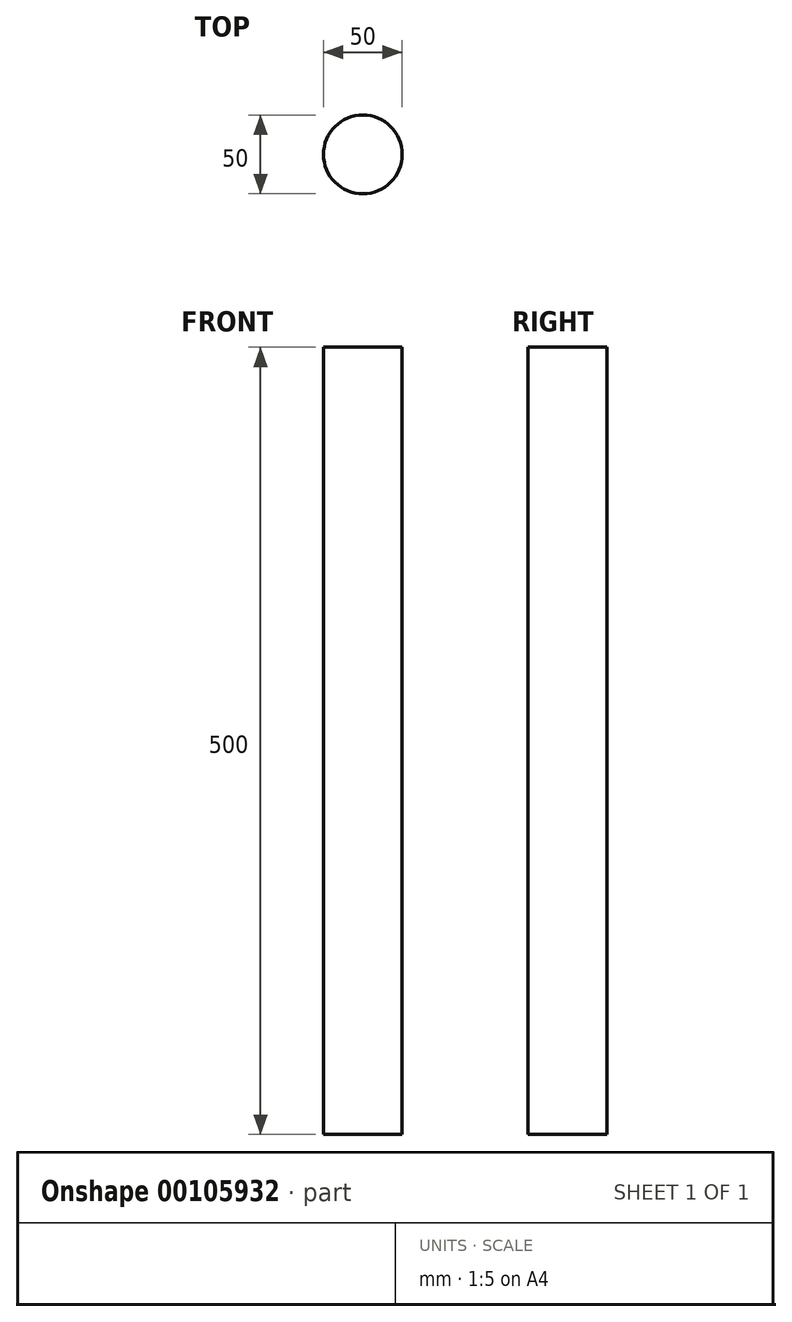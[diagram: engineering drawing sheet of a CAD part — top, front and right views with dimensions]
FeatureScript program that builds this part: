
annotation { "Feature Type Name" : "Feature", "Feature Type Description" : "" }
export const myFeature = defineFeature(function(context is Context, id is Id, definition is map)
    precondition{}
    {
        {
            var Q0;
            Q0=qCreatedBy(makeId("Top.planeOp"),FACE);
            var sketch = newSketch(context, id + "F0", { "sketchPlane" : qUnion([Q0])});
            skCircle(sketch, "E0", {"center": v(0, 0) * mm, "radius": 25 * mm});
            skSolve(sketch);
        }
        {
            var Q0;
            Q0=makeQuery(id+"F0.imprint","IMPRINT",FACE,{"disambiguationData":[TD([[makeQuery(id+"F0.imprint","IMPRINT",EDGE,{"derivedFrom":sQuery(id+"F0.wireOp",EDGE,"E0")}),1.0]])]});
            extrude(context, id + "F1", {"entities" : qUnion([Q0]), "depth" : 500 * mm});
        }
    });
